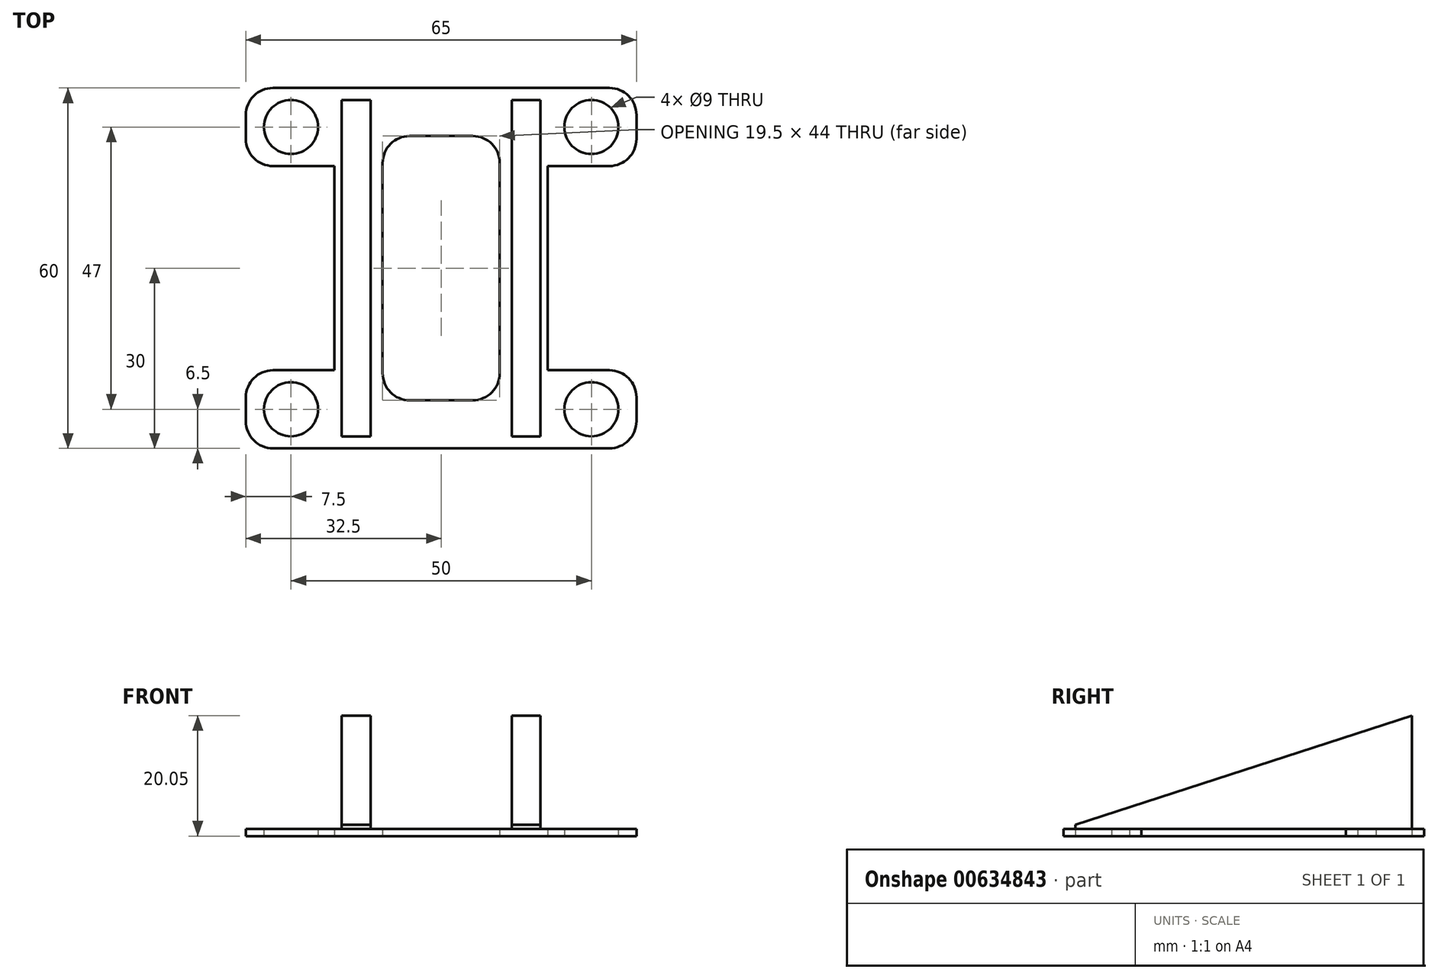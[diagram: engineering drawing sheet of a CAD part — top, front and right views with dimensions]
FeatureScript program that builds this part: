
annotation { "Feature Type Name" : "Feature", "Feature Type Description" : "" }
export const myFeature = defineFeature(function(context is Context, id is Id, definition is map)
    precondition{}
    {
        {
            var Q0;
            Q0=qCreatedBy(makeId("Top.planeOp"),FACE);
            var sketch = newSketch(context, id + "F0", { "sketchPlane" : qUnion([Q0])});
            skLineSegment(sketch, "E0.bottom", {"start": v(17.75, 30) * mm, "end": v(-17.75, 30) * mm});
            skLineSegment(sketch, "E0.top", {"start": v(17.75, -30) * mm, "end": v(-17.75, -30) * mm});
            skLineSegment(sketch, "E0.left", {"start": v(17.75, 30) * mm, "end": v(17.75, -30) * mm});
            skLineSegment(sketch, "E0.right", {"start": v(-17.75, 30) * mm, "end": v(-17.75, -30) * mm});
            skPoint(sketch, "E0.middle", {"position": v(0, 0) * mm});
            skCircle(sketch, "E1", {"center": v(25, 23.5) * mm, "radius": 4.5 * mm});
            skCircle(sketch, "E2.MirrorC", {"center": v(25, -23.5) * mm, "radius": 4.5 * mm});
            skCircle(sketch, "E3.MirrorC", {"center": v(-25, 23.5) * mm, "radius": 4.5 * mm});
            skCircle(sketch, "E4.MirrorC", {"center": v(-25, -23.5) * mm, "radius": 4.5 * mm});
            skLineSegment(sketch, "E5.bottom", {"start": v(-28, 30) * mm, "end": v(28, 30) * mm});
            skLineSegment(sketch, "E5.top", {"start": v(-28, 17) * mm, "end": v(28, 17) * mm});
            skLineSegment(sketch, "E5.left", {"start": v(-32.5, 25.5) * mm, "end": v(-32.5, 21.5) * mm});
            skLineSegment(sketch, "E5.right", {"start": v(32.5, 25.5) * mm, "end": v(32.5, 21.5) * mm});
            skPoint(sketch, "E6.visualSharp", {"position": v(-32.5, 30) * mm});
            skArc(sketch, "E6.filletArc", {"start": v(-28, 30) * mm, "mid": v(-31.18, 28.68) * mm, "end": v(-32.5, 25.5) * mm});
            skPoint(sketch, "E7.visualSharp", {"position": v(-32.5, 17) * mm});
            skArc(sketch, "E7.filletArc", {"start": v(-32.5, 21.5) * mm, "mid": v(-31.18, 18.32) * mm, "end": v(-28, 17) * mm});
            skPoint(sketch, "E8.visualSharp", {"position": v(32.5, 30) * mm});
            skArc(sketch, "E8.filletArc", {"start": v(32.5, 25.5) * mm, "mid": v(31.18, 28.68) * mm, "end": v(28, 30) * mm});
            skPoint(sketch, "E9.visualSharp", {"position": v(32.5, 17) * mm});
            skArc(sketch, "E9.filletArc", {"start": v(28, 17) * mm, "mid": v(31.18, 18.32) * mm, "end": v(32.5, 21.5) * mm});
            skLineSegment(sketch, "E10.MirrorCS", {"start": v(-28, -17) * mm, "end": v(28, -17) * mm});
            skArc(sketch, "E11.MirrorCS", {"start": v(-32.5, -21.5) * mm, "mid": v(-31.18, -18.32) * mm, "end": v(-28, -17) * mm});
            skLineSegment(sketch, "E12.MirrorCS", {"start": v(-32.5, -25.5) * mm, "end": v(-32.5, -21.5) * mm});
            skArc(sketch, "E13.MirrorCS", {"start": v(-28, -30) * mm, "mid": v(-31.18, -28.68) * mm, "end": v(-32.5, -25.5) * mm});
            skLineSegment(sketch, "E14.MirrorCS", {"start": v(-28, -30) * mm, "end": v(28, -30) * mm});
            skArc(sketch, "E15.MirrorCS", {"start": v(32.5, -25.5) * mm, "mid": v(31.18, -28.68) * mm, "end": v(28, -30) * mm});
            skLineSegment(sketch, "E16.MirrorCS", {"start": v(32.5, -25.5) * mm, "end": v(32.5, -21.5) * mm});
            skArc(sketch, "E17.MirrorCS", {"start": v(28, -17) * mm, "mid": v(31.18, -18.32) * mm, "end": v(32.5, -21.5) * mm});
            skLineSegment(sketch, "E18.bottom", {"start": v(5.25, 22) * mm, "end": v(-5.25, 22) * mm});
            skLineSegment(sketch, "E18.top", {"start": v(5.25, -22) * mm, "end": v(-5.25, -22) * mm});
            skLineSegment(sketch, "E18.left", {"start": v(9.75, 17.5) * mm, "end": v(9.75, -17.5) * mm});
            skLineSegment(sketch, "E18.right", {"start": v(-9.75, 17.5) * mm, "end": v(-9.75, -17.5) * mm});
            skPoint(sketch, "E19.visualSharp", {"position": v(-9.75, 22) * mm});
            skArc(sketch, "E19.filletArc", {"start": v(-5.25, 22) * mm, "mid": v(-8.43, 20.68) * mm, "end": v(-9.75, 17.5) * mm});
            skPoint(sketch, "E20.visualSharp", {"position": v(9.75, 22) * mm});
            skArc(sketch, "E20.filletArc", {"start": v(9.75, 17.5) * mm, "mid": v(8.43, 20.68) * mm, "end": v(5.25, 22) * mm});
            skPoint(sketch, "E21.visualSharp", {"position": v(9.75, -22) * mm});
            skArc(sketch, "E21.filletArc", {"start": v(5.25, -22) * mm, "mid": v(8.43, -20.68) * mm, "end": v(9.75, -17.5) * mm});
            skPoint(sketch, "E22.visualSharp", {"position": v(-9.75, -22) * mm});
            skArc(sketch, "E22.filletArc", {"start": v(-9.75, -17.5) * mm, "mid": v(-8.43, -20.68) * mm, "end": v(-5.25, -22) * mm});
            skSolve(sketch);
        }
        {
            var Q0;
            Q0=qSketchRegion(id+"F0",true);
            extrude(context, id + "F1", {"entities" : qUnion([Q0]), "depth" : 1.2 * mm, "offsetDistance" : 25 * mm});
        }
        {
            var Q0;
            Q0=makeQuery(id+"F1.opExtrude","CAP_FACE",FACE,{"disambiguationData":[OSD([sQuery(id+"F0.wireOp",EDGE,"E0.left"),sQuery(id+"F0.wireOp",EDGE,"E0.right"),sQuery(id+"F0.wireOp",EDGE,"E1"),sQuery(id+"F0.wireOp",EDGE,"E2.MirrorC"),sQuery(id+"F0.wireOp",EDGE,"E3.MirrorC"),sQuery(id+"F0.wireOp",EDGE,"E4.MirrorC"),sQuery(id+"F0.wireOp",EDGE,"E5.bottom"),sQuery(id+"F0.wireOp",EDGE,"E5.top"),sQuery(id+"F0.wireOp",EDGE,"E5.left"),sQuery(id+"F0.wireOp",EDGE,"E5.right"),sQuery(id+"F0.wireOp",EDGE,"E6.filletArc"),sQuery(id+"F0.wireOp",EDGE,"E7.filletArc"),sQuery(id+"F0.wireOp",EDGE,"E8.filletArc"),sQuery(id+"F0.wireOp",EDGE,"E9.filletArc"),sQuery(id+"F0.wireOp",EDGE,"E10.MirrorCS"),sQuery(id+"F0.wireOp",EDGE,"E11.MirrorCS"),sQuery(id+"F0.wireOp",EDGE,"E12.MirrorCS"),sQuery(id+"F0.wireOp",EDGE,"E13.MirrorCS"),sQuery(id+"F0.wireOp",EDGE,"E14.MirrorCS"),sQuery(id+"F0.wireOp",EDGE,"E15.MirrorCS"),sQuery(id+"F0.wireOp",EDGE,"E16.MirrorCS"),sQuery(id+"F0.wireOp",EDGE,"E17.MirrorCS"),sQuery(id+"F0.wireOp",EDGE,"E18.bottom"),sQuery(id+"F0.wireOp",EDGE,"E18.top"),sQuery(id+"F0.wireOp",EDGE,"E18.left"),sQuery(id+"F0.wireOp",EDGE,"E18.right"),sQuery(id+"F0.wireOp",EDGE,"E19.filletArc"),sQuery(id+"F0.wireOp",EDGE,"E20.filletArc"),sQuery(id+"F0.wireOp",EDGE,"E21.filletArc"),sQuery(id+"F0.wireOp",EDGE,"E22.filletArc")])],"isStart":false});
            var sketch = newSketch(context, id + "F2", { "sketchPlane" : qUnion([Q0])});
            skLineSegment(sketch, "E23.bottom", {"start": v(11.75, 28) * mm, "end": v(16.55, 28) * mm});
            skLineSegment(sketch, "E23.top", {"start": v(11.75, -28) * mm, "end": v(16.55, -28) * mm});
            skLineSegment(sketch, "E23.left", {"start": v(11.75, 28) * mm, "end": v(11.75, -28) * mm});
            skLineSegment(sketch, "E23.right", {"start": v(16.55, 28) * mm, "end": v(16.55, -28) * mm});
            skLineSegment(sketch, "E24.MirrorCS", {"start": v(-11.75, 28) * mm, "end": v(-11.75, -28) * mm});
            skLineSegment(sketch, "E25.MirrorCS", {"start": v(-11.75, 28) * mm, "end": v(-16.55, 28) * mm});
            skLineSegment(sketch, "E26.MirrorCS", {"start": v(-16.55, 28) * mm, "end": v(-16.55, -28) * mm});
            skLineSegment(sketch, "E27.MirrorCS", {"start": v(-11.75, -28) * mm, "end": v(-16.55, -28) * mm});
            skSolve(sketch);
        }
        {
            var Q0;
            Q0 = qSketchRegion(id + "F2", true);
            extrude(context, id + "F3", {"entities" : qUnion([Q0]), "operationType" : NewBodyOperationType.ADD, "depth" : 25 * mm, "offsetDistance" : 25 * mm});
        }
        {
            var Q0;
            Q0=makeQuery(id+"F1.opExtrude","CAP_EDGE",EDGE,{"disambiguationData":[OSD([sQuery(id+"F0.wireOp",EDGE,"E14.MirrorCS")])],"isStart":false});
            cPlane(context, id + "F4", {"entities" : qUnion([Q0]), "cplaneType" : CPlaneType.LINE_ANGLE, "offset" : 25 * mm, "angle" : 108 * degree, "width" : 150 * mm, "height" : 150 * mm});
        }
        {
            var Q0;
            Q0=qCreatedBy(id+"F4.planeOp",FACE);
            var sketch = newSketch(context, id + "F5", { "sketchPlane" : qUnion([Q0])});
            skLineSegment(sketch, "E28.bottom", {"start": v(-47.45, 47.96) * mm, "end": v(54.18, 47.96) * mm});
            skLineSegment(sketch, "E28.top", {"start": v(-47.45, -60.98) * mm, "end": v(54.18, -60.98) * mm});
            skLineSegment(sketch, "E28.left", {"start": v(-47.45, 47.96) * mm, "end": v(-47.45, -60.98) * mm});
            skLineSegment(sketch, "E28.right", {"start": v(54.18, 47.96) * mm, "end": v(54.18, -60.98) * mm});
            skSolve(sketch);
        }
        {
            var Q0;
            Q0 = qSketchRegion(id + "F5", true);
            extrude(context, id + "F6", {"entities" : qUnion([Q0]), "operationType" : NewBodyOperationType.REMOVE, "depth" : 50 * mm, "offsetDistance" : 25 * mm});
        }
    });
